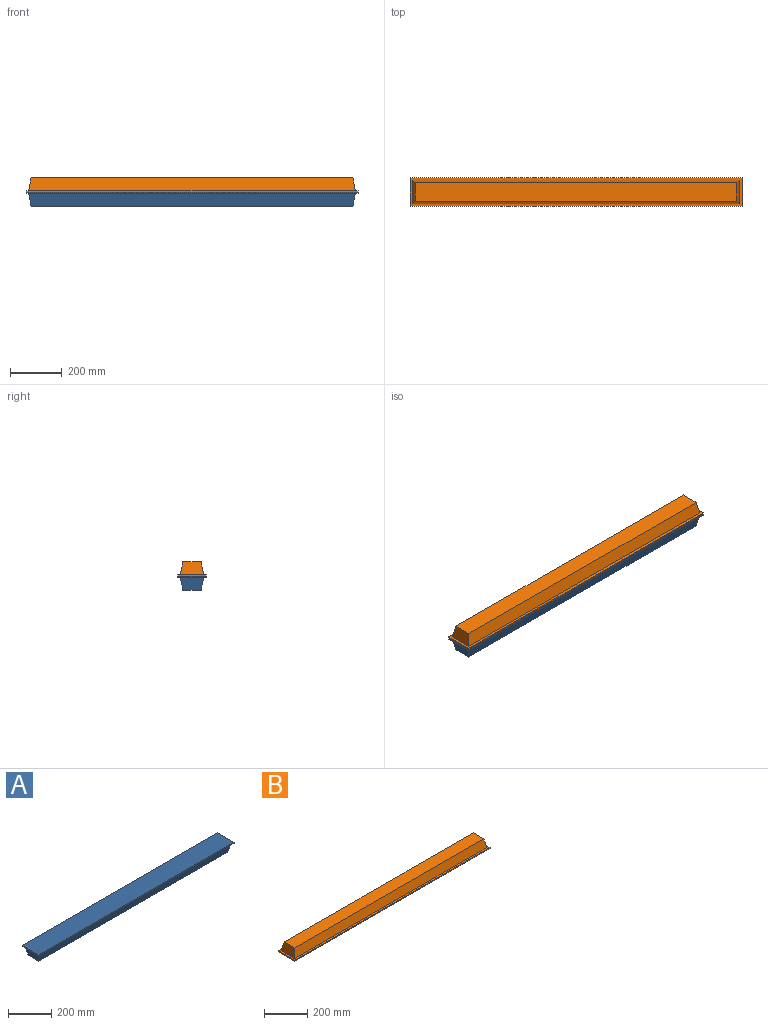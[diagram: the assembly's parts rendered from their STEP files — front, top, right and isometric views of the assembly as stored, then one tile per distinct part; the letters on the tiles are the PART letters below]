
ASSEMBLY  parts=2 mates=1
PART A: 11 faces, bbox 1280x110x55 mm
  f0: plane 1240x70mm, normal (0,0,-1), area 86800mm2, adj f1,f2,f9,f10
  f1: plane 1260x50mm, normal (0,-0.98,-0.2), area 63737.7mm2, adj f0,f6,f9,f10
  f2: plane 1260x50mm, normal (0,0.98,-0.2), area 63737.7mm2, adj f0,f6,f9,f10
  f3: plane 1280x5mm, normal (0,-1,0), area 6400mm2, adj f4,f6,f7,f8
  f4: plane 1280x110mm, normal (0,0,1), area 140800mm2, adj f3,f5,f7,f8
  f5: plane 1280x5mm, normal (0,1,0), area 6400mm2, adj f4,f6,f7,f8
  f6: plane 1280x110mm, normal (0,0,-1), area 27400mm2, adj f1,f2,f3,f5,f7,f8,f9,f10
  f7: plane 110x5mm, normal (1,0,0), area 550mm2, adj f3,f4,f5,f6
  f8: plane 110x5mm, normal (-1,0,0), area 550mm2, adj f3,f4,f5,f6
  f9: plane 90x50mm, normal (-0.98,0,-0.2), area 4079.2mm2, adj f0,f1,f2,f6
  f10: plane 90x50mm, normal (0.98,0,-0.2), area 4079.2mm2, adj f0,f1,f2,f6
PART B: 11 faces, bbox 1280x110x55 mm
  f0: plane 1240x70mm, normal (0,0,1), area 86800mm2, adj f1,f2,f9,f10
  f1: plane 1260x50mm, normal (0,-0.98,0.2), area 63737.7mm2, adj f0,f6,f9,f10
  f2: plane 1260x50mm, normal (0,0.98,0.2), area 63737.7mm2, adj f0,f6,f9,f10
  f3: plane 1280x5mm, normal (0,-1,0), area 6400mm2, adj f4,f6,f7,f8
  f4: plane 1280x110mm, normal (0,0,-1), area 140800mm2, adj f3,f5,f7,f8
  f5: plane 1280x5mm, normal (0,1,0), area 6400mm2, adj f4,f6,f7,f8
  f6: plane 1280x110mm, normal (0,0,1), area 27400mm2, adj f1,f2,f3,f5,f7,f8,f9,f10
  f7: plane 110x5mm, normal (1,0,0), area 550mm2, adj f3,f4,f5,f6
  f8: plane 110x5mm, normal (-1,0,0), area 550mm2, adj f3,f4,f5,f6
  f9: plane 90x50mm, normal (-0.98,0,0.2), area 4079.2mm2, adj f0,f1,f2,f6
  f10: plane 90x50mm, normal (0.98,0,0.2), area 4079.2mm2, adj f0,f1,f2,f6
PLACE A t=(-433.69,-71.46,268.4)mm
PLACE B t=(-433.69,-71.46,268.4)mm
MATE fastened A.f4 <-> B.f4  axis (0,0,1) through (-433.69,-71.46,268.4)mm
